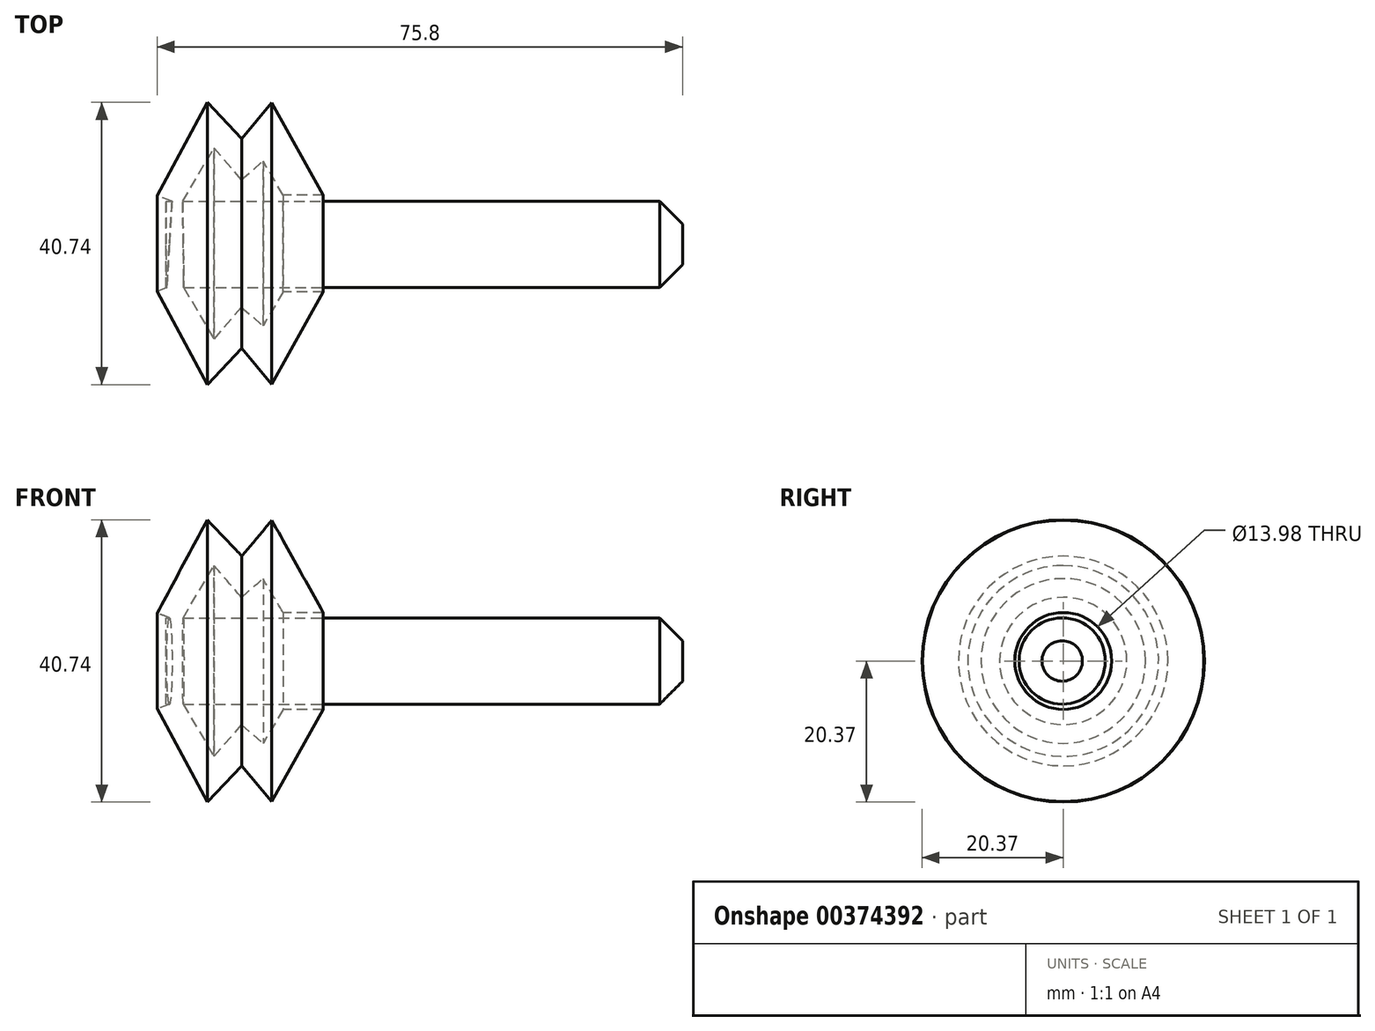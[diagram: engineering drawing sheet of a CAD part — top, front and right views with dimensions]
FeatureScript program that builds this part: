
annotation { "Feature Type Name" : "Feature", "Feature Type Description" : "" }
export const myFeature = defineFeature(function(context is Context, id is Id, definition is map)
    precondition{}
    {
        {
            var Q0;
            Q0=qCreatedBy(makeId("Top.planeOp"),FACE);
            var sketch = newSketch(context, id + "F0", { "sketchPlane" : qUnion([Q0])});
            skLineSegment(sketch, "E0", {"start": v(-20.43, 4.97) * mm, "end": v(-13.23, -8.5) * mm});
            skLineSegment(sketch, "E1", {"start": v(-13.23, -8.5) * mm, "end": v(-8.22, -3.25) * mm});
            skLineSegment(sketch, "E2", {"start": v(-8.22, -3.25) * mm, "end": v(-3.91, -8.41) * mm});
            skLineSegment(sketch, "E3", {"start": v(-3.91, -8.41) * mm, "end": v(3.52, 4.9) * mm});
            skLineSegment(sketch, "E4", {"start": v(3.52, 4.9) * mm, "end": v(-2.27, 4.9) * mm});
            skLineSegment(sketch, "E5", {"start": v(-2.27, 4.9) * mm, "end": v(-5.16, 0) * mm});
            skLineSegment(sketch, "E6", {"start": v(-5.16, 0) * mm, "end": v(-8.3, 2.7) * mm});
            skLineSegment(sketch, "E7", {"start": v(-8.3, 2.7) * mm, "end": v(-12.25, -1.9) * mm});
            skLineSegment(sketch, "E8", {"start": v(-12.25, -1.9) * mm, "end": v(-17.06, 6.3) * mm});
            skLineSegment(sketch, "E9", {"start": v(-17.06, 6.3) * mm, "end": v(-20.43, 4.97) * mm});
            skLineSegment(sketch, "E10", {"start": v(-14.76, 11.88) * mm, "end": v(-5.1, 11.88) * mm});
            skSolve(sketch);
        }
        {
            var Q0;
            Q0=makeQuery(id+"F0.imprint","IMPRINT",FACE,{"disambiguationData":[TD([[makeQuery(id+"F0.imprint","IMPRINT",EDGE,{"derivedFrom":sQuery(id+"F0.wireOp",EDGE,"E0")}),1.0]])]});
            var Q1;
            Q1=sQuery(id+"F0.wireOp",EDGE,"E10");
            revolve(context, id + "F1", {"entities" : qUnion([Q0]), "axis" : qUnion([Q1]), "revolveType" : RevolveType.FULL});
        }
        {
            var Q0;
            Q0=qCreatedBy(makeId("Right.planeOp"),FACE);
            var sketch = newSketch(context, id + "F2", { "sketchPlane" : qUnion([Q0])});
            skCircle(sketch, "E11", {"center": v(11.73, 0) * mm, "radius": 6.22 * mm});
            skSolve(sketch);
        }
        {
            var Q0;
            Q0=makeQuery(id+"F2.imprint","IMPRINT",FACE,{"disambiguationData":[TD([[makeQuery(id+"F2.imprint","IMPRINT",EDGE,{"derivedFrom":sQuery(id+"F2.wireOp",EDGE,"E11")}),1.0]])]});
            extrude(context, id + "F3", {"entities" : qUnion([Q0]), "operationType" : NewBodyOperationType.ADD, "oppositeDirection" : true, "depth" : 19.15 * mm});
        }
        {
            var Q0;
            Q0=makeQuery(id+"F3.opExtrude","CAP_FACE",FACE,{"disambiguationData":[OSD([sQuery(id+"F2.wireOp",EDGE,"E11")])],"isStart":true});
            extrude(context, id + "F4", {"entities" : qUnion([Q0]), "operationType" : NewBodyOperationType.ADD, "depth" : 55.37 * mm});
        }
        {
            var Q0;
            Q0=makeQuery(id+"F4.opExtrude","CAP_FACE",FACE,{"disambiguationData":[OSD([sQuery(id+"F2.wireOp",EDGE,"E11")])],"isStart":false});
            chamfer(context, id + "F5", {"entities" : qUnion([Q0]), "width" : 3.3 * mm, "tangentPropagation" : true});
        }
        {
            var Q0;
            Q0=qCreatedBy(makeId("Front.planeOp"),FACE);
            var sketch = newSketch(context, id + "F6", { "sketchPlane" : qUnion([Q0])});
            skLineSegment(sketch, "E12", {"start": v(40.22, -16.02) * mm, "end": v(40.22, -33.48) * mm});
            skLineSegment(sketch, "E13", {"start": v(72.25, 7.61) * mm, "end": v(72.25, -11) * mm});
            skSolve(sketch);
        }
        {
            var Q0;
            Q0=qCreatedBy(makeId("Front.planeOp"),FACE);
            var sketch = newSketch(context, id + "F7", { "sketchPlane" : qUnion([Q0])});
            skCircle(sketch, "E14", {"center": v(70.8, 0) * mm, "radius": 3.47 * mm});
            skSolve(sketch);
        }
        {
            var Q0;
            Q0=sQuery(id+"F7.wireOp",EDGE,"E14");
            var Q1;
            Q1=sQuery(id+"F6.wireOp",EDGE,"E12");
            revolve(context, id + "F8", {"bodyType" : ToolBodyType.SURFACE, "surfaceEntities" : qUnion([Q0]), "axis" : qUnion([Q1]), "revolveType" : RevolveType.FULL});
        }
    });
